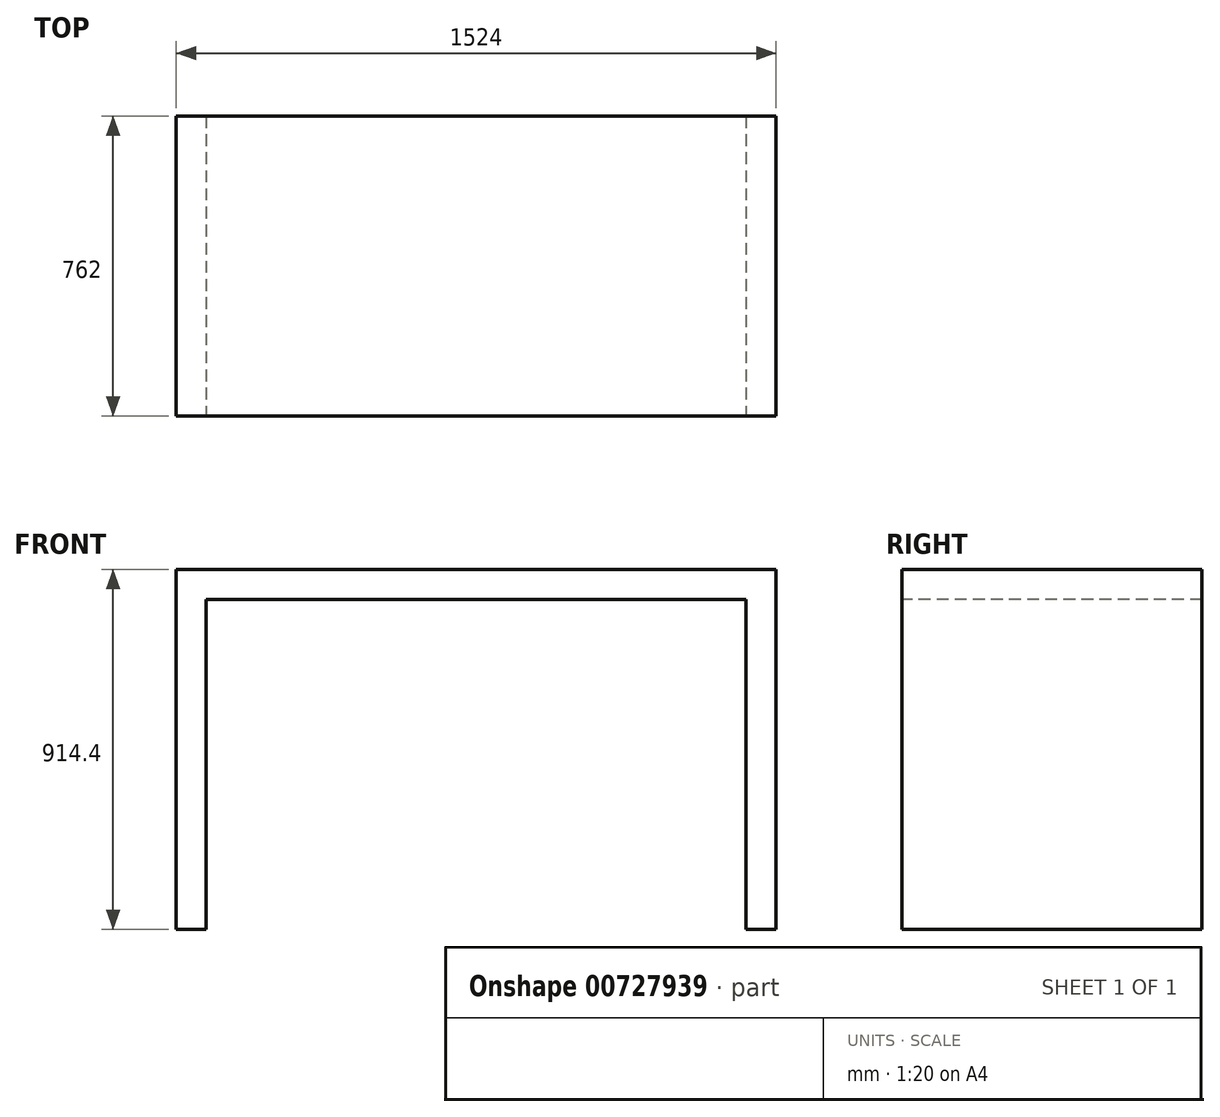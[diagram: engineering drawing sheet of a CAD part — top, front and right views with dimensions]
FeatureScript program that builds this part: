
annotation { "Feature Type Name" : "Feature", "Feature Type Description" : "" }
export const myFeature = defineFeature(function(context is Context, id is Id, definition is map)
    precondition{}
    {
        {
            var Q0;
            Q0=qCreatedBy(makeId("Top.planeOp"),FACE);
            var sketch = newSketch(context, id + "F0", { "sketchPlane" : qUnion([Q0])});
            skLineSegment(sketch, "E0.bottom", {"start": v(762, -381) * mm, "end": v(-762, -381) * mm});
            skLineSegment(sketch, "E0.top", {"start": v(762, 381) * mm, "end": v(-762, 381) * mm});
            skLineSegment(sketch, "E0.left", {"start": v(762, -381) * mm, "end": v(762, 381) * mm});
            skLineSegment(sketch, "E0.right", {"start": v(-762, -381) * mm, "end": v(-762, 381) * mm});
            skPoint(sketch, "E0.middle", {"position": v(0, 0) * mm});
            skSolve(sketch);
        }
        {
            var Q0;
            Q0 = qSketchRegion(id + "F0", true);
            extrude(context, id + "F1", {"entities" : qUnion([Q0]), "depth" : 914.4 * mm, "offsetDistance" : 25.4 * mm});
        }
        {
            var Q0;
            Q0=makeQuery(id+"F1.opExtrude","SWEPT_FACE",FACE,{"disambiguationData":[OSD([sQuery(id+"F0.wireOp",EDGE,"E0.bottom")])]});
            var sketch = newSketch(context, id + "F2", { "sketchPlane" : qUnion([Q0])});
            skLineSegment(sketch, "E1.bottom", {"start": v(-685.8, 838.2) * mm, "end": v(685.8, 838.2) * mm});
            skLineSegment(sketch, "E1.top", {"start": v(-685.8, 0) * mm, "end": v(685.8, 0) * mm});
            skLineSegment(sketch, "E1.left", {"start": v(-685.8, 838.2) * mm, "end": v(-685.8, 0) * mm});
            skLineSegment(sketch, "E1.right", {"start": v(685.8, 838.2) * mm, "end": v(685.8, 0) * mm});
            skSolve(sketch);
        }
        {
            var Q0;
            Q0 = qSketchRegion(id + "F2", true);
            extrude(context, id + "F3", {"entities" : qUnion([Q0]), "operationType" : NewBodyOperationType.REMOVE, "endBound" : BoundingType.THROUGH_ALL, "oppositeDirection" : true, "depth" : 25.4 * mm, "offsetDistance" : 25.4 * mm});
        }
    });
